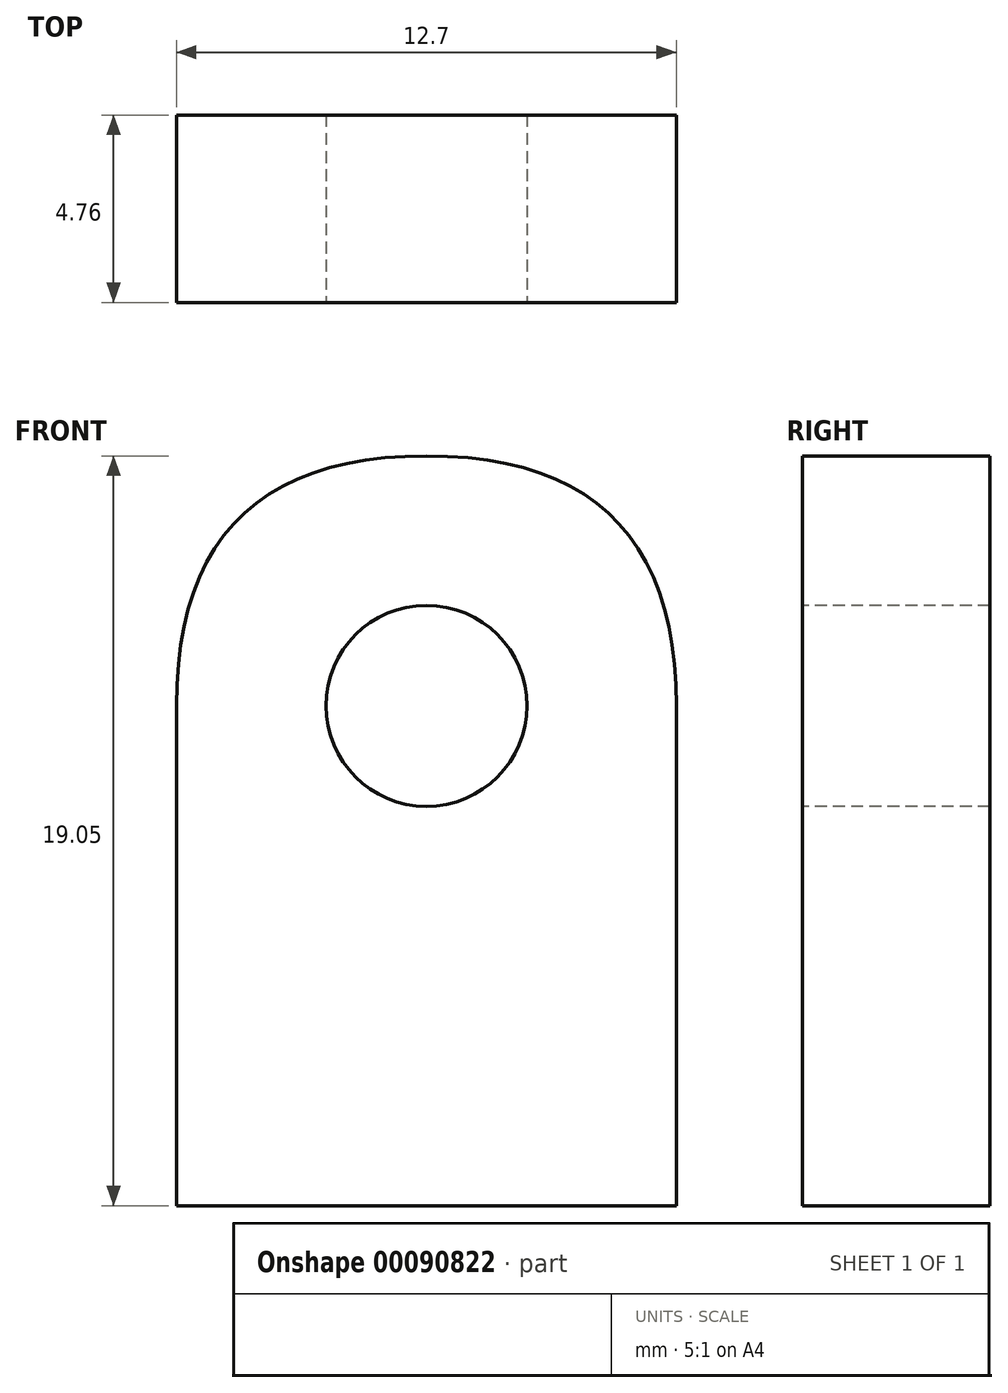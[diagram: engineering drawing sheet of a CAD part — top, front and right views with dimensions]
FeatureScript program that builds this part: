
annotation { "Feature Type Name" : "Feature", "Feature Type Description" : "" }
export const myFeature = defineFeature(function(context is Context, id is Id, definition is map)
    precondition{}
    {
        {
            var Q0;
            Q0=qCreatedBy(makeId("Right.planeOp"),FACE);
            var sketch = newSketch(context, id + "F0", { "sketchPlane" : qUnion([Q0])});
            skLineSegment(sketch, "E0.bottom", {"start": v(4.76, -19.05) * mm, "end": v(0, -19.05) * mm});
            skLineSegment(sketch, "E0.right", {"start": v(0, -19.05) * mm, "end": v(0, 0) * mm});
            skPoint(sketch, "E0.middle", {"position": v(0, 0) * mm});
            skLineSegment(sketch, "E1.0", {"start": v(4.76, -19.05) * mm, "end": v(4.76, 0) * mm});
            skLineSegment(sketch, "E2", {"start": v(0, 0) * mm, "end": v(4.76, 0) * mm});
            skPoint(sketch, "E3.visualSharp", {"position": v(0, -19.05) * mm});
            skSolve(sketch);
        }
        {
            var Q0;
            Q0=makeQuery(id+"F0.imprint","IMPRINT",FACE,{"disambiguationData":[TD([[makeQuery(id+"F0.imprint","IMPRINT",EDGE,{"derivedFrom":sQuery(id+"F0.wireOp",EDGE,"E0.bottom")}),-1.0]])]});
            extrude(context, id + "F1", {"entities" : qUnion([Q0]), "depth" : 12.7 * mm});
        }
        {
            var Q0;
            Q0=makeQuery(id+"F1.opExtrude","SWEPT_FACE",FACE,{"disambiguationData":[OSD([sQuery(id+"F0.wireOp",EDGE,"E0.right")])]});
            var sketch = newSketch(context, id + "F2", { "sketchPlane" : qUnion([Q0])});
            skPoint(sketch, "E4", {"position": v(6.35, -6.35) * mm});
            skSolve(sketch);
        }
        {
            var Q0;
            Q0=makeQuery(id+"F1.opExtrude","CAP_EDGE",EDGE,{"disambiguationData":[OSD([sQuery(id+"F0.wireOp",EDGE,"E2")])],"isStart":true});
            var Q1;
            Q1=makeQuery(id+"F1.opExtrude","CAP_EDGE",EDGE,{"disambiguationData":[OSD([sQuery(id+"F0.wireOp",EDGE,"E2")])],"isStart":false});
            fillet(context, id + "F3", {"entities" : qUnion([Q0, Q1]), "radius" : 6.35 * mm, "tangentPropagation" : true, "rho" : 0.5, "crossSection" : FilletCrossSection.CONIC, "allowEdgeOverflow" : false});
        }
        {
            var Q0;
            Q0=sQuery(id+"F2.wireOp",VERTEX,"E4");
            var Q1;
            Q1=makeQuery(id+"F1.opExtrude","SWEPT_BODY",BODY,{"disambiguationData":[OSD([sQuery(id+"F0.wireOp",EDGE,"E0.bottom"),sQuery(id+"F0.wireOp",EDGE,"E0.right"),sQuery(id+"F0.wireOp",EDGE,"E1.0"),sQuery(id+"F0.wireOp",EDGE,"8302332a-3770-464d-93ba-a0c0480e0648.0"),sQuery(id+"F0.wireOp",EDGE,"E2"),sQuery(id+"F0.wireOp",EDGE,"CodiWmq2-6aJ5-zft9-Cagu-XDMTQpmfyBpK")])]});
            hole(context, id + "F4", {"style" : HoleStyle.SIMPLE, "endStyle" : HoleEndStyle.THROUGH, "standardTappedOrClearance" : lookupTablePath({ "standard" : "ANSI", "engagement" : "75%", "pitch" : "20 tpi", "size" : "1/4", "type" : "Tapped" }), "standardBlindInLast" : lookupTablePath({ "standard" : "ANSI", "engagement" : "75%", "pitch" : "20 tpi", "size" : "1/4", "type" : "Tapped" }), "holeDiameter" : 5.1 * mm, "locations" : qUnion([Q0]), "scope" : qUnion([Q1]), "isTappedThrough" : true, "majorDiameter" : 6.35 * mm, "showTappedDepth" : true});
        }
        {
            var Q0;
            Q0=makeQuery(id+"F1.opExtrude","SWEPT_FACE",FACE,{"disambiguationData":[OSD([sQuery(id+"F0.wireOp",EDGE,"E0.bottom")])]});
            var sketch = newSketch(context, id + "F5", { "sketchPlane" : qUnion([Q0])});
            skLineSegment(sketch, "E5", {"start": v(12.7, -2.38) * mm, "end": v(0, -2.38) * mm, "construction": true});
            skLineSegment(sketch, "E6", {"start": v(6.35, 0) * mm, "end": v(6.35, -4.76) * mm, "construction": true});
            skPoint(sketch, "E7", {"position": v(6.35, -2.38) * mm});
            skSolve(sketch);
        }
    });
